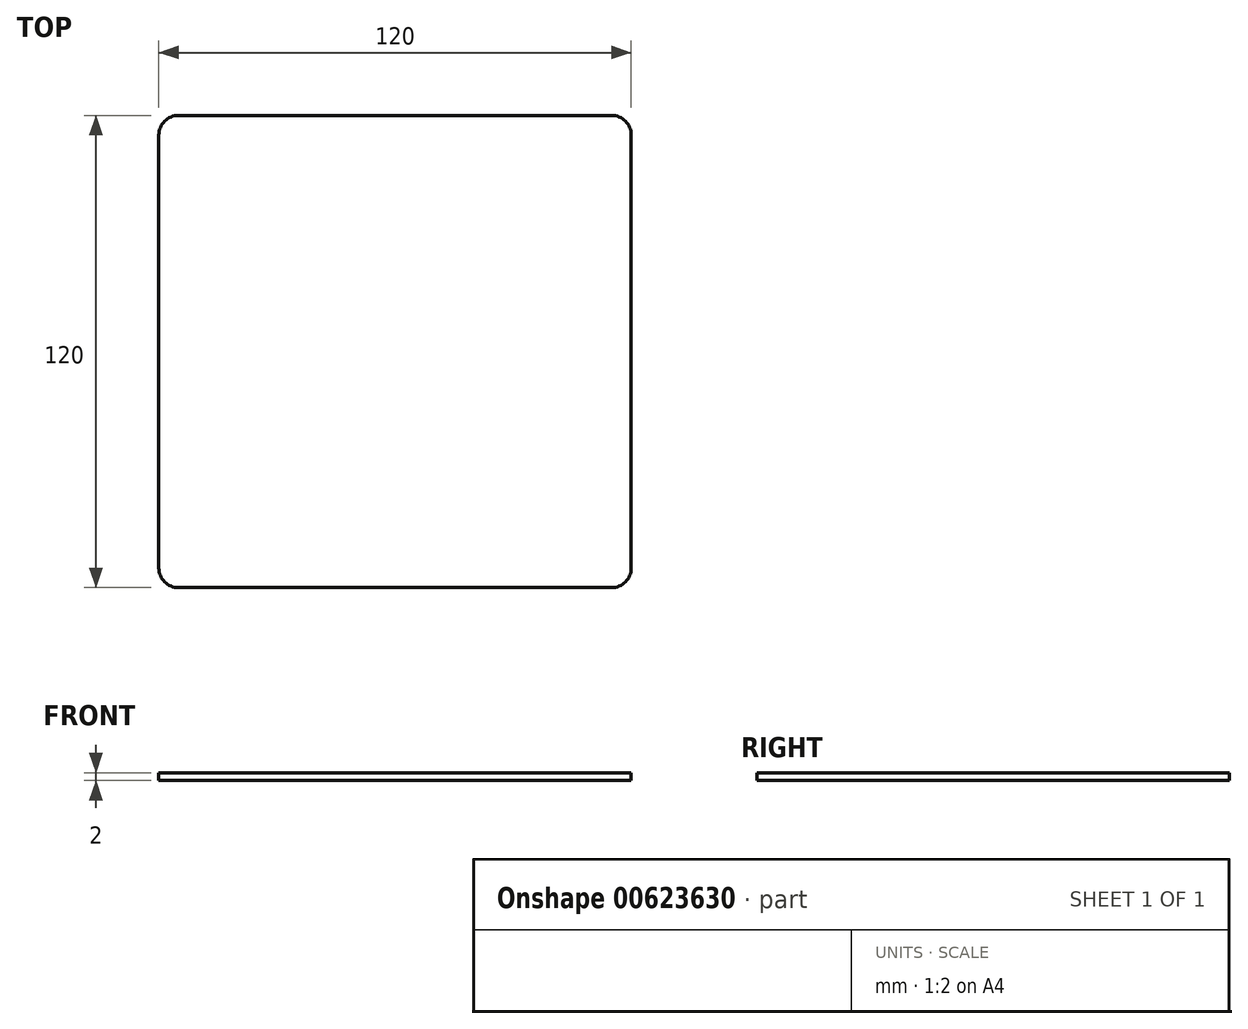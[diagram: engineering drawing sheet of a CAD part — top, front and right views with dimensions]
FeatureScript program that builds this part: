
annotation { "Feature Type Name" : "Feature", "Feature Type Description" : "" }
export const myFeature = defineFeature(function(context is Context, id is Id, definition is map)
    precondition{}
    {
        {
            var Q0;
            Q0=qCreatedBy(makeId("Top.planeOp"),FACE);
            var sketch = newSketch(context, id + "F0", { "sketchPlane" : qUnion([Q0])});
            skLineSegment(sketch, "E0.bottom", {"start": v(60, -60) * mm, "end": v(-60, -60) * mm});
            skLineSegment(sketch, "E0.top", {"start": v(60, 60) * mm, "end": v(-60, 60) * mm});
            skLineSegment(sketch, "E0.left", {"start": v(60, -60) * mm, "end": v(60, 60) * mm});
            skLineSegment(sketch, "E0.right", {"start": v(-60, -60) * mm, "end": v(-60, 60) * mm});
            skPoint(sketch, "E0.middle", {"position": v(0, 0) * mm});
            skSolve(sketch);
        }
        {
            var Q0;
            Q0=makeQuery(id+"F0.imprint","IMPRINT",FACE,{"disambiguationData":[TD([[makeQuery(id+"F0.imprint","IMPRINT",EDGE,{"derivedFrom":sQuery(id+"F0.wireOp",EDGE,"E0.bottom")}),-1.0]])]});
            extrude(context, id + "F1", {"entities" : qUnion([Q0]), "depth" : 2 * mm, "offsetDistance" : 25 * mm});
        }
        {
            var Q0;
            Q0=makeQuery(id+"F1.opExtrude","SWEPT_EDGE",EDGE,{"disambiguationData":[OSD([sQuery(id+"F0.wireOp",EDGE,"E0.top"),sQuery(id+"F0.wireOp",EDGE,"E0.right")])]});
            var Q1;
            Q1=makeQuery(id+"F1.opExtrude","SWEPT_EDGE",EDGE,{"disambiguationData":[OSD([sQuery(id+"F0.wireOp",EDGE,"E0.bottom"),sQuery(id+"F0.wireOp",EDGE,"E0.right")])]});
            var Q2;
            Q2=makeQuery(id+"F1.opExtrude","SWEPT_EDGE",EDGE,{"disambiguationData":[OSD([sQuery(id+"F0.wireOp",EDGE,"E0.bottom"),sQuery(id+"F0.wireOp",EDGE,"E0.left")])]});
            var Q3;
            Q3=makeQuery(id+"F1.opExtrude","SWEPT_EDGE",EDGE,{"disambiguationData":[OSD([sQuery(id+"F0.wireOp",EDGE,"E0.top"),sQuery(id+"F0.wireOp",EDGE,"E0.left")])]});
            fillet(context, id + "F2", {"entities" : qUnion([Q0, Q1, Q2, Q3]), "radius" : 5 * mm, "tangentPropagation" : true, "allowEdgeOverflow" : false});
        }
    });
